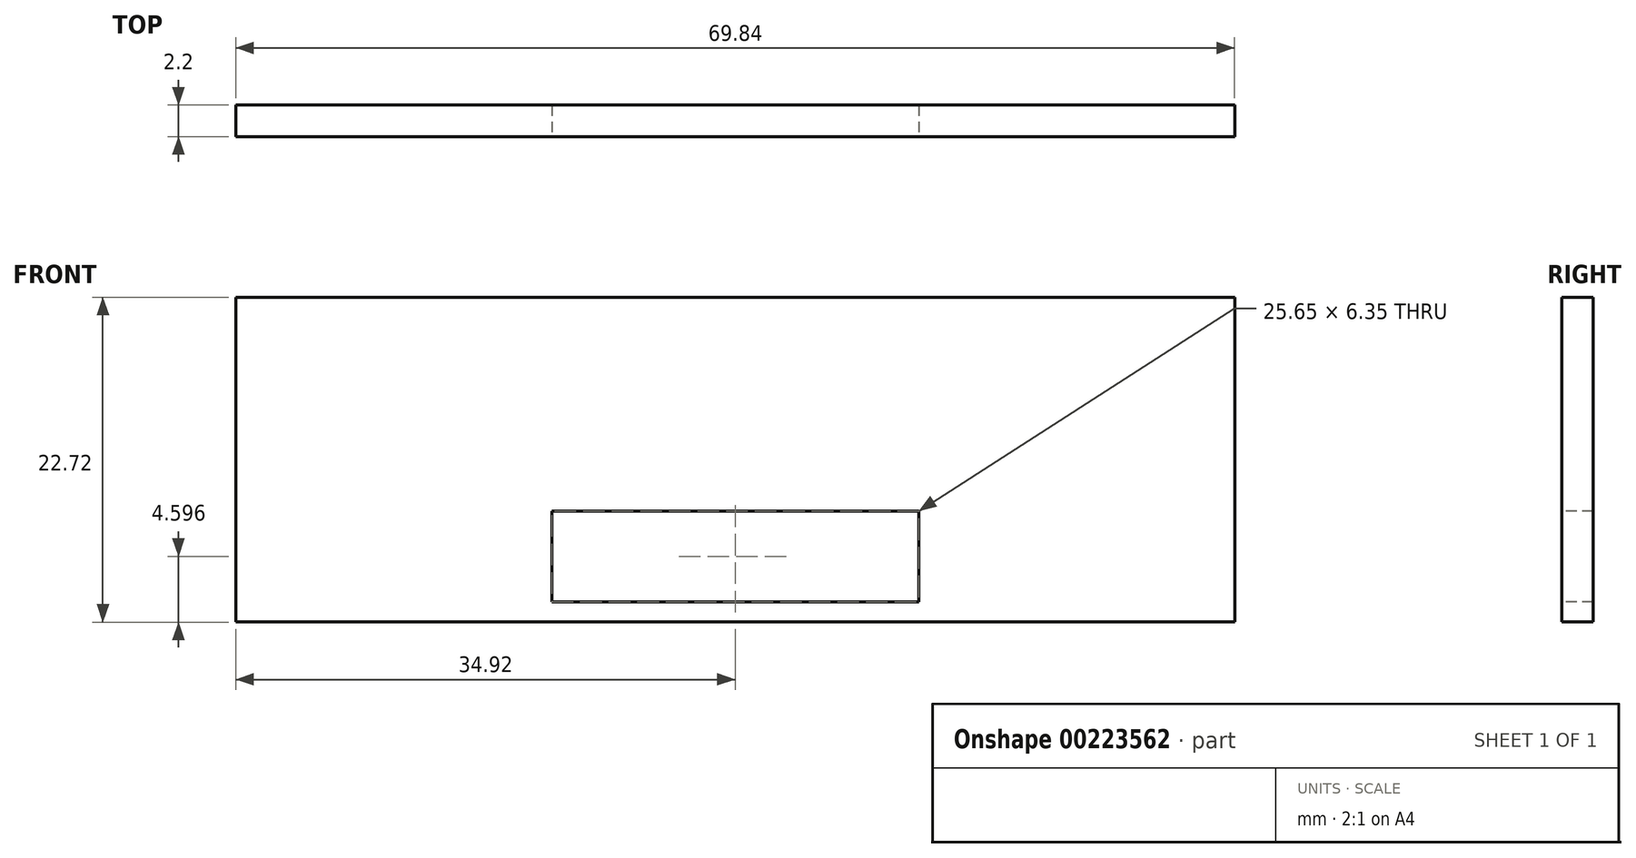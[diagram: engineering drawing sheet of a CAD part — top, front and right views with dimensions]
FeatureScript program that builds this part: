
annotation { "Feature Type Name" : "Feature", "Feature Type Description" : "" }
export const myFeature = defineFeature(function(context is Context, id is Id, definition is map)
    precondition{}
    {
        {
            var Q0;
            Q0=qCreatedBy(makeId("Front.planeOp"),FACE);
            var sketch = newSketch(context, id + "F0", { "sketchPlane" : qUnion([Q0])});
            skLineSegment(sketch, "E0.bottom", {"start": v(34.93, -11.36) * mm, "end": v(-34.93, -11.36) * mm});
            skLineSegment(sketch, "E0.top", {"start": v(34.93, 11.36) * mm, "end": v(-34.93, 11.36) * mm});
            skLineSegment(sketch, "E0.left", {"start": v(34.93, -11.36) * mm, "end": v(34.93, 11.36) * mm});
            skLineSegment(sketch, "E0.right", {"start": v(-34.93, -11.36) * mm, "end": v(-34.93, 11.36) * mm});
            skPoint(sketch, "E0.middle", {"position": v(0, 0) * mm});
            skSolve(sketch);
        }
        {
            var Q0;
            Q0=makeQuery(id+"F0.imprint","IMPRINT",FACE,{"disambiguationData":[TD([[makeQuery(id+"F0.imprint","IMPRINT",EDGE,{"derivedFrom":sQuery(id+"F0.wireOp",EDGE,"E0.bottom")}),-1.0]])]});
            extrude(context, id + "F1", {"entities" : qUnion([Q0]), "depth" : 2.2 * mm});
        }
        {
            var Q0;
            Q0=makeQuery(id+"F1.opExtrude","CAP_FACE",FACE,{"disambiguationData":[OSD([sQuery(id+"F0.wireOp",EDGE,"E0.bottom"),sQuery(id+"F0.wireOp",EDGE,"E0.top"),sQuery(id+"F0.wireOp",EDGE,"E0.left"),sQuery(id+"F0.wireOp",EDGE,"E0.right")])],"isStart":false});
            var sketch = newSketch(context, id + "F2", { "sketchPlane" : qUnion([Q0])});
            skLineSegment(sketch, "E1.bottom", {"start": v(12.83, 3.59) * mm, "end": v(-12.83, 3.59) * mm});
            skLineSegment(sketch, "E1.top", {"start": v(12.83, 9.94) * mm, "end": v(-12.83, 9.94) * mm});
            skLineSegment(sketch, "E1.left", {"start": v(12.83, 3.59) * mm, "end": v(12.83, 9.94) * mm});
            skLineSegment(sketch, "E1.right", {"start": v(-12.83, 3.59) * mm, "end": v(-12.83, 9.94) * mm});
            skPoint(sketch, "E1.middle", {"position": v(0, 6.76) * mm});
            skLineSegment(sketch, "E2.MirrorCS", {"start": v(12.83, -3.59) * mm, "end": v(-12.83, -3.59) * mm});
            skLineSegment(sketch, "E3.MirrorCS", {"start": v(12.83, -9.94) * mm, "end": v(-12.83, -9.94) * mm});
            skLineSegment(sketch, "E4.MirrorCS", {"start": v(12.83, -3.59) * mm, "end": v(12.83, -9.94) * mm});
            skLineSegment(sketch, "E5.MirrorCS", {"start": v(-12.83, -3.59) * mm, "end": v(-12.83, -9.94) * mm});
            skSolve(sketch);
        }
        {
            var Q0;
            Q0=makeQuery(id+"F2.imprint","IMPRINT",FACE,{"disambiguationData":[TD([[makeQuery(id+"F2.imprint","IMPRINT",EDGE,{"derivedFrom":sQuery(id+"F2.wireOp",EDGE,"E2.MirrorCS")}),1.0]])]});
            extrude(context, id + "F3", {"entities" : qUnion([Q0]), "operationType" : NewBodyOperationType.REMOVE, "oppositeDirection" : true, "depth" : 25.4 * mm});
        }
    });
